# Revit family: Sauna-Room_Prefab_Finlandia_FPF-57
name_source: partatom
category: Specialty Equipment
units: mm (PartAtom-declared; Revit-internal decimal feet)

## family parameters
Always vertical = No
Classification Number = 23.40.50.34.37
Cut with Voids When Loaded = No
Enable Cutting in Views = No
Maintain Annotation Orientation = No
Part Type = Normal
Room Calculation Point = No
Round Connector Dimension = Use Diameter
Shared = No
Work Plane-Based = Yes

## types (2) — shared parameters
Assembly Code = F1010300
Capacity = 4 People
Construction Details = http://www.arcat.com
Default Elevation = 0' - 0"
Description = Finlandia Prefab Modular Sauna Room - FPF 57 as Specified
Door RO Width = 2' - 2"
Green Building-LEED = http://www.arcat.com
Keynote = 13052
LBRLO = 0' - 0"
LBRRO = 0' - 0"
Manufacturer = Finlandia Sauna Products, Inc.
Manufacturer Fax = 503-684-1120
Manufacturer Website = http://www.finlandiasauna.com
Model = FPF 57
Product Data = http://www.arcat.com
Revision = R1_2014-07
Sales Information = http://www.finlandiasauna.com
Send Message = http://www.arcat.com
Specification = http://www.arcat.com
UBRLO = 0' - 0"
UBRRO = 0' - 0"
URL = http://www.finlandiasauna.com
Unit Depth = 5' - 0"
Unit Height = 7' - 1"
Unit Width = 7' - 0"
Wall Thickness = 0' - 2 1/2"
zero-valued in all types: Expected Lifespan (Years), Maintenance Schedule (Months), Warranty Duration (Years)

## per-type parameters (varying)
| type | DoorOffset | Reversed | Standard |
| Indoor Reversed as Specified | 2' - 8" | Yes | No |
| Indoor Standard as Specified | 2' - 2" | No | Yes |

## geometry (parser evidence)
native form markers: Blend x12, Sweep x6
no freeform markers — native parametric forms only
